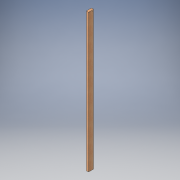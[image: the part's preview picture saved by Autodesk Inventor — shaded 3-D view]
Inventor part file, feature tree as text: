
AUTODESK INVENTOR PART (.ipt)
format: ipt  version: 2016 (Build 200138000, 138)  size: 121,856 bytes
history: native  units: in
note: dims shown in document units (in); Inventor stores cm internally (conversion verified against a paired STEP export)
features: extrude x3, sketch x3
ambient origin geometry x8: Origin, YZ Plane, XZ Plane, XY Plane, X Axis, Y Axis, Z Axis, Center Point
bodies: Solid1 (feature_tree)
feature tree (6):
  extrude  "Extrusion1"  Depth=3.5in
  extrude  "Extrusion4"  Depth=94.5in
  extrude  "Extrusion5"  Depth=1.5in
  sketch  "Sketch1"  dims[d0=1.5in d1=3.5in]
  sketch  "Sketch4"  dims[d2=94.5in d3=0.0in d12=0.1875in]
  sketch  "Sketch5"  dims[d13=1.5in d14=0.0in d15=1.5in d16=0.1875in d17=1.5in d18=0.0in]
